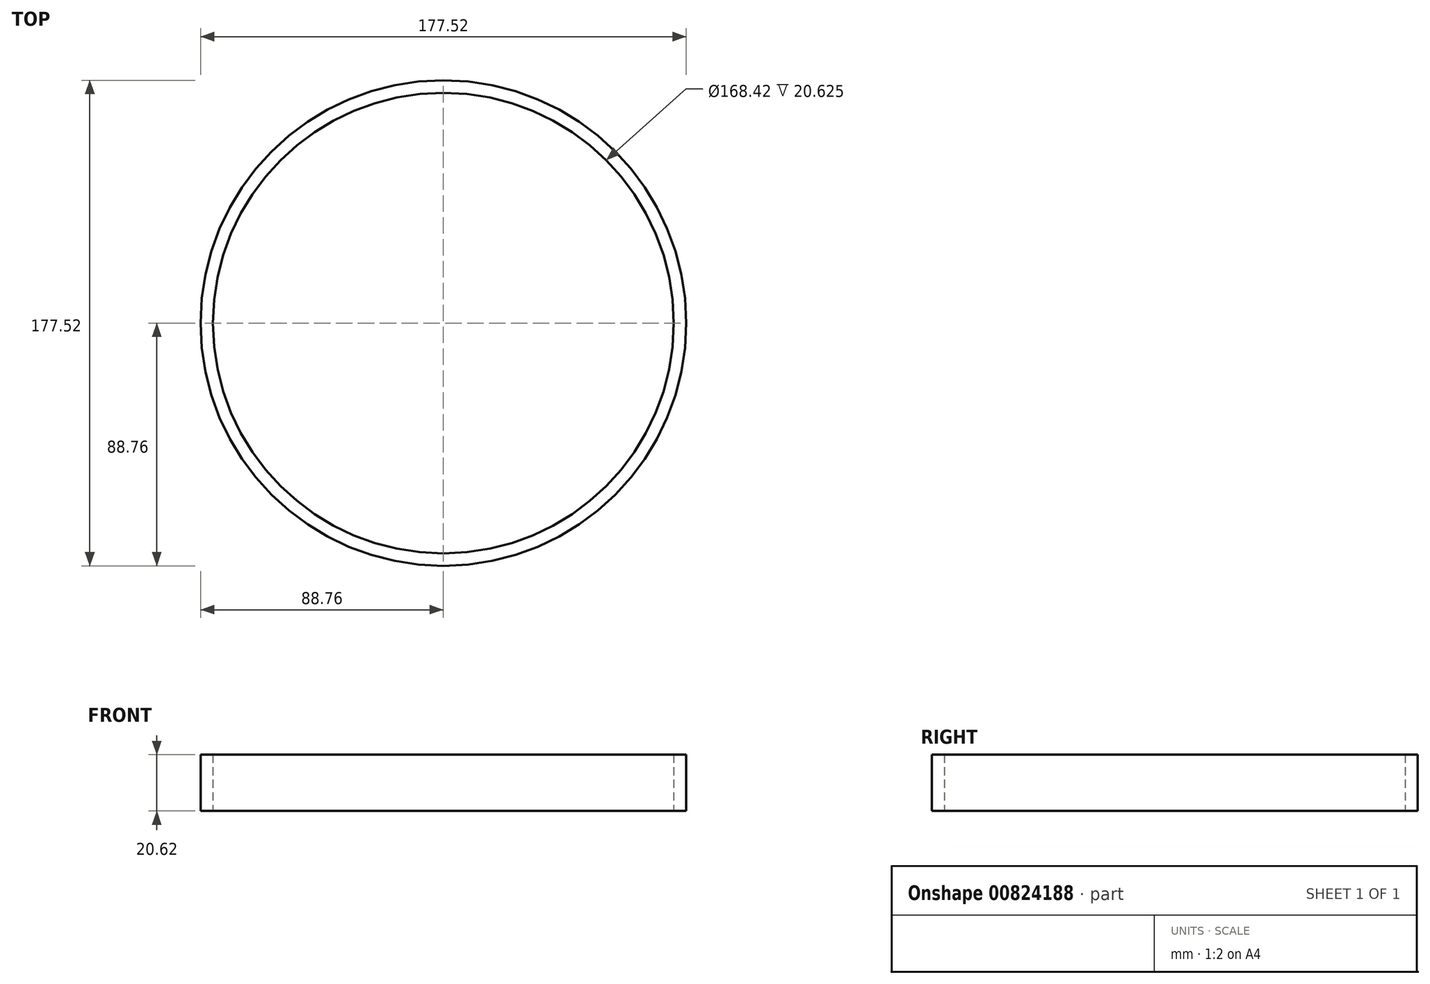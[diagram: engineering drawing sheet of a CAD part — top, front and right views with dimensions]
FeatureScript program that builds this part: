
annotation { "Feature Type Name" : "Feature", "Feature Type Description" : "" }
export const myFeature = defineFeature(function(context is Context, id is Id, definition is map)
    precondition{}
    {
        {
            var Q0;
            Q0=qCreatedBy(makeId("Top.planeOp"),FACE);
            var sketch = newSketch(context, id + "F0", { "sketchPlane" : qUnion([Q0])});
            skCircle(sketch, "E0", {"center": v(0, 0) * mm, "radius": 88.76 * mm});
            skCircle(sketch, "E1", {"center": v(0, 0) * mm, "radius": 84.21 * mm});
            skSolve(sketch);
        }
        {
            var Q0;
            Q0=makeQuery(id+"F0.imprint","IMPRINT",FACE,{"disambiguationData":[TD([[makeQuery(id+"F0.imprint","IMPRINT",EDGE,{"derivedFrom":sQuery(id+"F0.wireOp",EDGE,"E0")}),1.0]])]});
            extrude(context, id + "F1", {"entities" : qUnion([Q0]), "depth" : 20.62 * mm, "offsetDistance" : 25.4 * mm});
        }
    });
